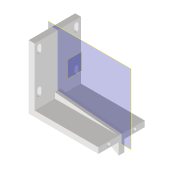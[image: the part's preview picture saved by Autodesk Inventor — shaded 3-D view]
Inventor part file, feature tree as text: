
AUTODESK INVENTOR PART (.ipt)
format: ipt  version: 2022 (Build 260153000, 153)  size: 174,080 bytes
history: native  units: mm
features: extrude x4, sketch x4, reference x4, projected_geometry x3, plane x2, other x2
ambient origin geometry x8: Origin, YZ Plane, XZ Plane, XY Plane, X Axis, Y Axis, Z Axis, Center Point
bodies: Volumenkörper1 (feature_tree)
feature tree (19):
  plane  "Arbeitsebene1"
  extrude  "Extrusion1"  Depth=5.0mm TaperAngle=0.0deg
  extrude  "Extrusion2"  Depth=55.0mm TaperAngle=0.0deg
  plane  "Arbeitsebene2"
  extrude  "Extrusion3"  Depth=5.0mm
  extrude  "Extrusion4"  Depth=5.0mm
  sketch  "Skizze1"  dims[d0=15.0mm d1=5.0mm d2=0.0mm]
  reference  "Referenz1"
  reference  "Referenz2"
  reference  "Referenz3"
  reference  "Referenz4"
  sketch  "Skizze2"  dims[d3=5.0mm d4=55.0mm d5=0.0mm]
  projected_geometry  "Projizierte Kontur1"
  sketch  "Skizze3"  dims[d6=-20.0mm d7=5.0mm]
  projected_geometry  "Projizierte Kontur2"
  sketch  "Skizze4"  dims[d8=5.0mm d9=0.0mm d10=2.8mm d11=2.8mm d12=0.0mm d13=0.0mm d14=8.0mm d15=60.0deg]
  projected_geometry  "Projizierte Kontur3"
  other  "Assembly_XYZ_Stage_Micrometer_ontop.iam"
  other  "00_XYZstage_micro_LT-4047-S1:1"
